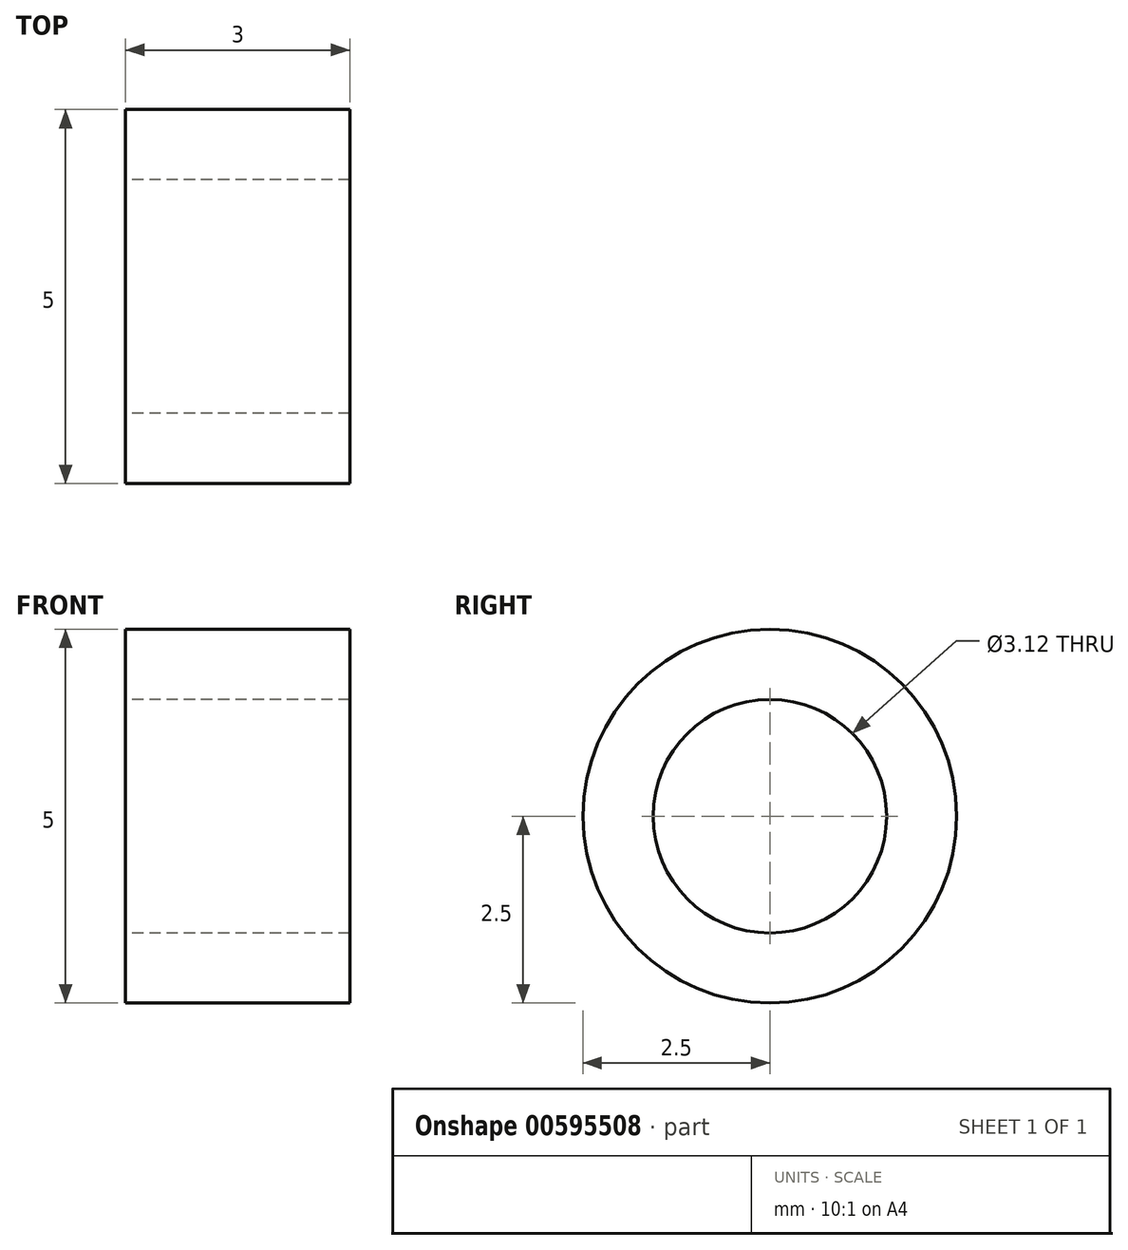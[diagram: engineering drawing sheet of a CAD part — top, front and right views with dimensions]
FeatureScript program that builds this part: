
annotation { "Feature Type Name" : "Feature", "Feature Type Description" : "" }
export const myFeature = defineFeature(function(context is Context, id is Id, definition is map)
    precondition{}
    {
        {
            var Q0;
            Q0=qCreatedBy(makeId("Right.planeOp"),FACE);
            var sketch = newSketch(context, id + "F0", { "sketchPlane" : qUnion([Q0])});
            skCircle(sketch, "E0", {"center": v(0, 0) * mm, "radius": 2.5 * mm});
            skCircle(sketch, "E1", {"center": v(0, 0) * mm, "radius": 1.56 * mm});
            skSolve(sketch);
        }
        {
            var Q0;
            Q0=makeQuery(id+"F0.imprint","IMPRINT",FACE,{"disambiguationData":[TD([[makeQuery(id+"F0.imprint","IMPRINT",EDGE,{"derivedFrom":sQuery(id+"F0.wireOp",EDGE,"E0")}),1.0]])]});
            extrude(context, id + "F1", {"entities" : qUnion([Q0]), "depth" : 3 * mm, "offsetDistance" : 25 * mm});
        }
    });
